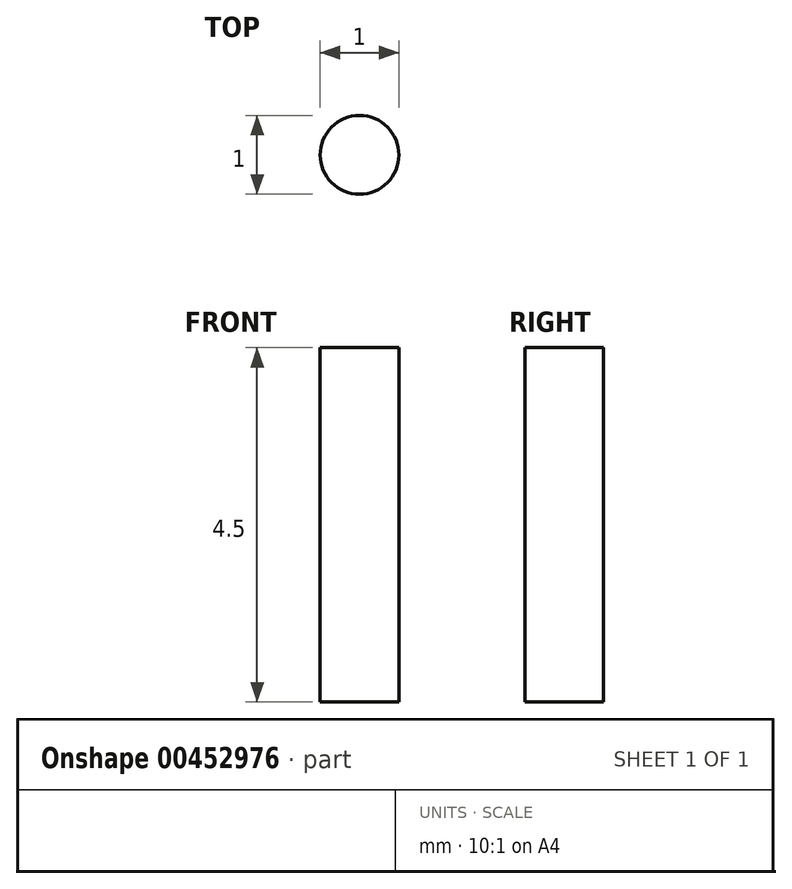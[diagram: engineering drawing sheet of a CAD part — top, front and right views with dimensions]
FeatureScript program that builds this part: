
annotation { "Feature Type Name" : "Feature", "Feature Type Description" : "" }
export const myFeature = defineFeature(function(context is Context, id is Id, definition is map)
    precondition{}
    {
        {
            var Q0;
            Q0=qCreatedBy(makeId("Top.planeOp"),FACE);
            var sketch = newSketch(context, id + "F0", { "sketchPlane" : qUnion([Q0])});
            skCircle(sketch, "E0", {"center": v(0, 0) * mm, "radius": 0.5 * mm});
            skSolve(sketch);
        }
        {
            var Q0;
            Q0=makeQuery(id+"F0.imprint","IMPRINT",FACE,{"disambiguationData":[TD([[makeQuery(id+"F0.imprint","IMPRINT",EDGE,{"derivedFrom":sQuery(id+"F0.wireOp",EDGE,"E0")}),1.0]])]});
            extrude(context, id + "F1", {"entities" : qUnion([Q0]), "depth" : 4.5 * mm, "offsetDistance" : 25 * mm});
        }
    });
